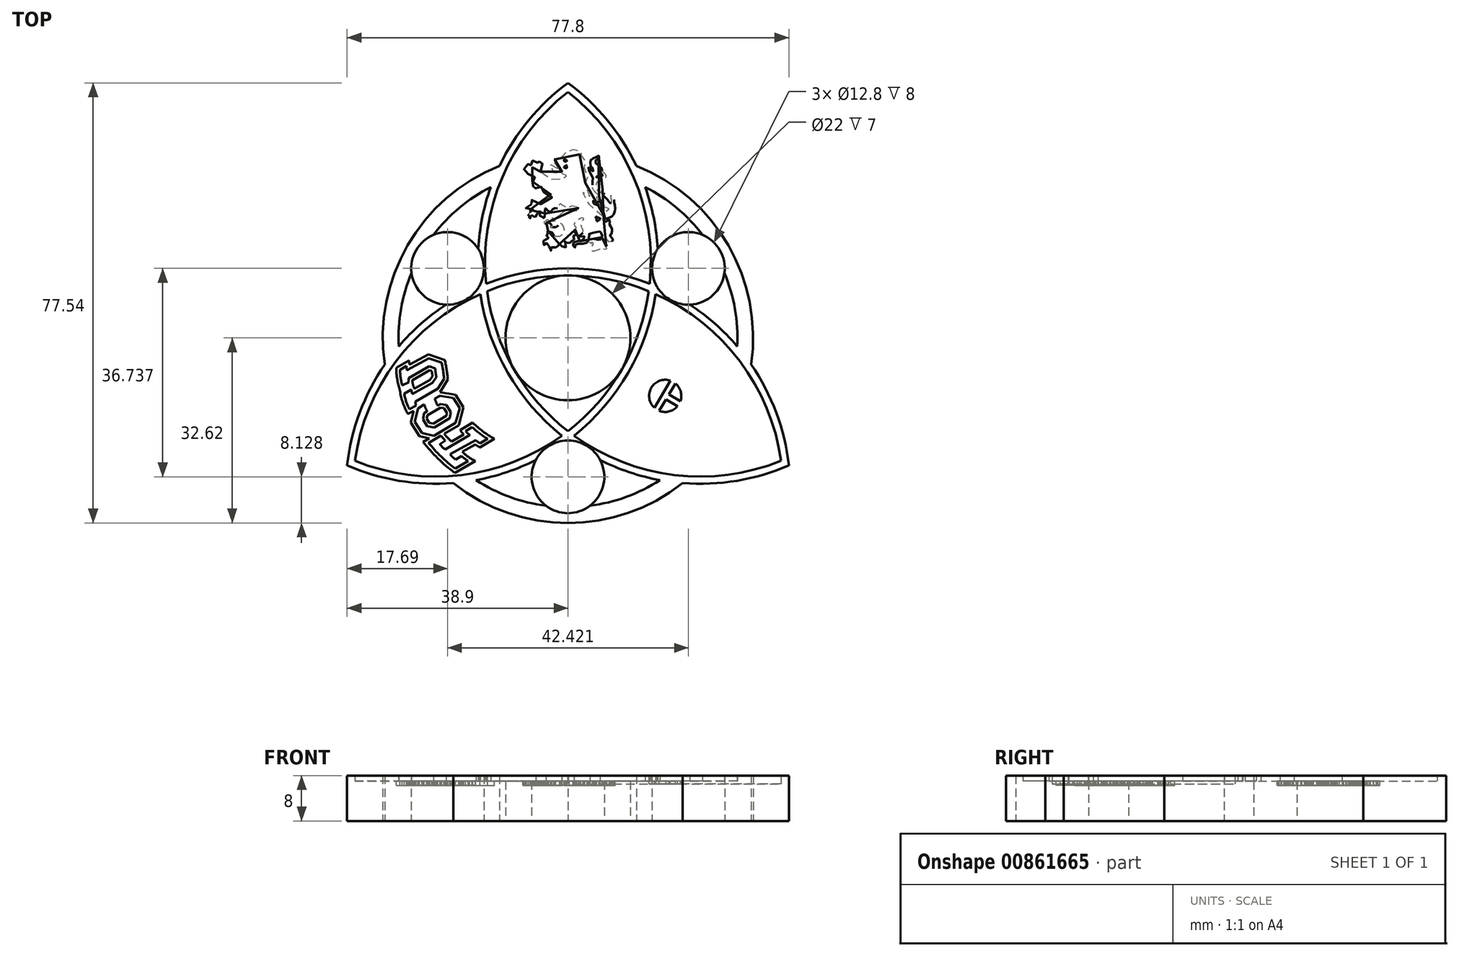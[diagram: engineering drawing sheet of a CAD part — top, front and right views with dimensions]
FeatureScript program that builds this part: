
annotation { "Feature Type Name" : "Feature", "Feature Type Description" : "" }
export const myFeature = defineFeature(function(context is Context, id is Id, definition is map)
    precondition{}
    {
        {
            var Q0;
            Q0=qCreatedBy(makeId("Top.planeOp"),FACE);
            var sketch = newSketch(context, id + "F0", { "sketchPlane" : qUnion([Q0])});
            skCircle(sketch, "E0", {"center": v(0, 0) * mm, "radius": 11 * mm});
            skArc(sketch, "E1", {"start": v(-13, 28.27) * mm, "mid": v(-26.95, 15.56) * mm, "end": v(-30.98, -2.89) * mm});
            skArc(sketch, "E2", {"start": v(0, 44.4) * mm, "mid": v(-7.94, 37.5) * mm, "end": v(-13, 28.27) * mm});
            skArc(sketch, "E3.MirrorCS", {"start": v(0, 44.4) * mm, "mid": v(7.94, 37.5) * mm, "end": v(13, 28.27) * mm});
            skArc(sketch, "E4.1.0", {"start": v(-38.45, -22.2) * mm, "mid": v(-28.5, -25.62) * mm, "end": v(-17.99, -25.39) * mm});
            skArc(sketch, "E4.1.1", {"start": v(-38.45, -22.2) * mm, "mid": v(-36.44, -11.88) * mm, "end": v(-30.98, -2.89) * mm});
            skArc(sketch, "E4.2.0", {"start": v(38.45, -22.2) * mm, "mid": v(36.44, -11.88) * mm, "end": v(30.98, -2.89) * mm});
            skArc(sketch, "E4.2.1", {"start": v(38.45, -22.2) * mm, "mid": v(28.5, -25.62) * mm, "end": v(17.99, -25.39) * mm});
            skArc(sketch, "E5.trimOffspring", {"start": v(-17.99, -25.39) * mm, "mid": v(0, -31.12) * mm, "end": v(17.99, -25.39) * mm});
            skArc(sketch, "E6.trimOffspring", {"start": v(30.98, -2.89) * mm, "mid": v(26.95, 15.56) * mm, "end": v(13, 28.27) * mm});
            skSolve(sketch);
        }
        {
            var Q0;
            Q0=qSketchRegion(id+"F0",true);
            extrude(context, id + "F1", {"entities" : qUnion([Q0]), "depth" : 7 * mm, "offsetDistance" : 25.4 * mm});
        }
        {
            var Q0;
            Q0=makeQuery(id+"F1.opExtrude","CAP_FACE",FACE,{"disambiguationData":[OSD([sQuery(id+"F0.wireOp",EDGE,"E0"),sQuery(id+"F0.wireOp",EDGE,"E1"),sQuery(id+"F0.wireOp",EDGE,"E2"),sQuery(id+"F0.wireOp",EDGE,"E3.MirrorCS"),sQuery(id+"F0.wireOp",EDGE,"E4.1.0"),sQuery(id+"F0.wireOp",EDGE,"E4.1.1"),sQuery(id+"F0.wireOp",EDGE,"E4.2.0"),sQuery(id+"F0.wireOp",EDGE,"E4.2.1"),sQuery(id+"F0.wireOp",EDGE,"E5.trimOffspring"),sQuery(id+"F0.wireOp",EDGE,"E6.trimOffspring")])],"isStart":false});
            var sketch = newSketch(context, id + "F2", { "sketchPlane" : qUnion([Q0])});
            skArc(sketch, "E7.0.1", {"start": v(-18.03, -25.36) * mm, "mid": v(0, -31.12) * mm, "end": v(18.03, -25.36) * mm});
            skArc(sketch, "E7.0.4", {"start": v(30.98, -2.94) * mm, "mid": v(26.95, 15.56) * mm, "end": v(12.95, 28.3) * mm});
            skArc(sketch, "E7.0.7", {"start": v(-12.95, 28.3) * mm, "mid": v(-26.95, 15.56) * mm, "end": v(-30.98, -2.94) * mm});
            skArc(sketch, "E8.2", {"start": v(-13.6, 26.56) * mm, "mid": v(-25.85, 14.92) * mm, "end": v(-29.8, -1.5) * mm});
            skArc(sketch, "E8.3", {"start": v(29.8, -1.5) * mm, "mid": v(25.85, 14.92) * mm, "end": v(13.6, 26.56) * mm});
            skArc(sketch, "E8.7", {"start": v(-16.2, -25.07) * mm, "mid": v(0, -29.85) * mm, "end": v(16.2, -25.07) * mm});
            skArc(sketch, "E9", {"start": v(0, 43.33) * mm, "mid": v(-11.57, 28.3) * mm, "end": v(-14.4, 9.53) * mm});
            skArc(sketch, "E10", {"start": v(-37.52, -21.66) * mm, "mid": v(-18.71, -24.17) * mm, "end": v(-1.05, -17.23) * mm});
            skArc(sketch, "E11", {"start": v(37.52, -21.66) * mm, "mid": v(30.29, -4.12) * mm, "end": v(15.45, 7.7) * mm});
            skArc(sketch, "E12.0", {"start": v(0, 44.92) * mm, "mid": v(-7.61, 37.5) * mm, "end": v(-12.95, 28.3) * mm});
            skArc(sketch, "E13.0", {"start": v(-38.9, -22.46) * mm, "mid": v(-28.67, -25.34) * mm, "end": v(-18.03, -25.36) * mm});
            skArc(sketch, "E14.0", {"start": v(38.9, -22.46) * mm, "mid": v(36.28, -12.16) * mm, "end": v(30.98, -2.94) * mm});
            skPoint(sketch, "E15.orphan", {"position": v(-13, 28.27) * mm});
            skPoint(sketch, "E16.orphan", {"position": v(13, 28.27) * mm});
            skArc(sketch, "E17.trimOffspring", {"start": v(-13.6, 26.56) * mm, "mid": v(-15.62, 17.9) * mm, "end": v(-15.62, 9.02) * mm});
            skArc(sketch, "E18.trimOffspring", {"start": v(12.95, 28.3) * mm, "mid": v(7.61, 37.5) * mm, "end": v(0, 44.92) * mm});
            skArc(sketch, "E19.trimOffspring", {"start": v(-15.62, 9.02) * mm, "mid": v(-23.32, 4.57) * mm, "end": v(-29.8, -1.5) * mm});
            skArc(sketch, "E20.trimOffspring", {"start": v(-15.45, 7.7) * mm, "mid": v(-30.29, -4.12) * mm, "end": v(-37.52, -21.66) * mm});
            skArc(sketch, "E21.trimOffspring", {"start": v(-15.45, 7.7) * mm, "mid": v(-10.63, -6.14) * mm, "end": v(-1.05, -17.23) * mm});
            skArc(sketch, "E22.trimOffspring", {"start": v(-14.24, 8.22) * mm, "mid": v(-9.53, -5.5) * mm, "end": v(0, -16.44) * mm});
            skArc(sketch, "E23.trimOffspring", {"start": v(14.4, 9.53) * mm, "mid": v(11.57, 28.3) * mm, "end": v(0, 43.33) * mm});
            skArc(sketch, "E24.trimOffspring", {"start": v(14.4, 9.53) * mm, "mid": v(0, 12.27) * mm, "end": v(-14.4, 9.53) * mm});
            skArc(sketch, "E25.trimOffspring", {"start": v(14.24, 8.22) * mm, "mid": v(0, 11) * mm, "end": v(-14.24, 8.22) * mm});
            skArc(sketch, "E26.trimOffspring", {"start": v(15.62, 9.02) * mm, "mid": v(15.62, 17.9) * mm, "end": v(13.6, 26.56) * mm});
            skArc(sketch, "E27.trimOffspring", {"start": v(0, -18.04) * mm, "mid": v(7.7, -22.48) * mm, "end": v(16.2, -25.07) * mm});
            skArc(sketch, "E28.trimOffspring", {"start": v(0, -16.44) * mm, "mid": v(9.53, -5.5) * mm, "end": v(14.24, 8.22) * mm});
            skArc(sketch, "E29.trimOffspring", {"start": v(1.05, -17.23) * mm, "mid": v(18.71, -24.17) * mm, "end": v(37.52, -21.66) * mm});
            skArc(sketch, "E30.trimOffspring", {"start": v(1.05, -17.23) * mm, "mid": v(10.63, -6.14) * mm, "end": v(15.45, 7.7) * mm});
            skPoint(sketch, "E31.orphan", {"position": v(-30.98, -2.89) * mm});
            skPoint(sketch, "E32.orphan", {"position": v(-17.99, -25.39) * mm});
            skArc(sketch, "E33.trimOffspring", {"start": v(-30.98, -2.94) * mm, "mid": v(-36.28, -12.16) * mm, "end": v(-38.9, -22.46) * mm});
            skArc(sketch, "E34.trimOffspring", {"start": v(-16.2, -25.07) * mm, "mid": v(-7.7, -22.48) * mm, "end": v(0, -18.04) * mm});
            skPoint(sketch, "E35.orphan", {"position": v(30.98, -2.89) * mm});
            skPoint(sketch, "E36.orphan", {"position": v(17.99, -25.39) * mm});
            skArc(sketch, "E37.trimOffspring", {"start": v(18.03, -25.36) * mm, "mid": v(28.67, -25.34) * mm, "end": v(38.9, -22.46) * mm});
            skArc(sketch, "E38.trimOffspring", {"start": v(29.8, -1.5) * mm, "mid": v(23.32, 4.57) * mm, "end": v(15.62, 9.02) * mm});
            skSolve(sketch);
        }
        {
            var Q0;
            Q0=qSketchRegion(id+"F2",true);
            extrude(context, id + "F3", {"entities" : qUnion([Q0]), "operationType" : NewBodyOperationType.ADD, "depth" : 1 * mm, "offsetDistance" : 25.4 * mm});
        }
        {
            var Q0;
            Q0=makeQuery(id+"F3.boolean.opBoolean","SPLIT",FACE,{"disambiguationData":[TD([makeQuery(id+"F3.opExtrude","SWEPT_FACE",FACE,{"disambiguationData":[OSD([sQuery(id+"F2.wireOp",EDGE,"E10")])]}),makeQuery(id+"F3.opExtrude","SWEPT_FACE",FACE,{"disambiguationData":[OSD([sQuery(id+"F2.wireOp",EDGE,"E20.trimOffspring")])]}),makeQuery(id+"F3.opExtrude","SWEPT_FACE",FACE,{"disambiguationData":[OSD([sQuery(id+"F2.wireOp",EDGE,"E21.trimOffspring")])]})])],"derivedFrom":makeQuery(id+"F1.opExtrude","CAP_FACE",FACE,{"disambiguationData":[OSD([sQuery(id+"F0.wireOp",EDGE,"E0"),sQuery(id+"F0.wireOp",EDGE,"E1"),sQuery(id+"F0.wireOp",EDGE,"E2"),sQuery(id+"F0.wireOp",EDGE,"E3.MirrorCS"),sQuery(id+"F0.wireOp",EDGE,"E4.1.0"),sQuery(id+"F0.wireOp",EDGE,"E4.1.1"),sQuery(id+"F0.wireOp",EDGE,"E4.2.0"),sQuery(id+"F0.wireOp",EDGE,"E4.2.1"),sQuery(id+"F0.wireOp",EDGE,"E5.trimOffspring"),sQuery(id+"F0.wireOp",EDGE,"E6.trimOffspring")])],"isStart":false})});
            var sketch = newSketch(context, id + "F4", { "sketchPlane" : qUnion([Q0])});
            skArc(sketch, "E39.0.0", {"start": v(-37.99, -17.38) * mm, "mid": v(-35.23, -9.8) * mm, "end": v(-30.98, -2.94) * mm});
            skArc(sketch, "E39.0.1", {"start": v(-30.98, -2.94) * mm, "mid": v(-30.98, -2.91) * mm, "end": v(-30.98, -2.89) * mm});
            skArc(sketch, "E39.0.2", {"start": v(-30.98, -2.89) * mm, "mid": v(-35.48, -9.65) * mm, "end": v(-37.99, -17.38) * mm});
            skArc(sketch, "E40.0.0", {"start": v(-17.99, -25.39) * mm, "mid": v(-18.01, -25.37) * mm, "end": v(-18.03, -25.36) * mm});
            skArc(sketch, "E40.0.1", {"start": v(-18.03, -25.36) * mm, "mid": v(-26.1, -25.61) * mm, "end": v(-34.05, -24.2) * mm});
            skArc(sketch, "E40.0.2", {"start": v(-34.05, -24.2) * mm, "mid": v(-26.1, -25.9) * mm, "end": v(-17.99, -25.39) * mm});
            skArc(sketch, "E41.0.0", {"start": v(34.05, -24.2) * mm, "mid": v(26.1, -25.61) * mm, "end": v(18.03, -25.36) * mm});
            skArc(sketch, "E41.0.1", {"start": v(18.03, -25.36) * mm, "mid": v(18.01, -25.37) * mm, "end": v(17.99, -25.39) * mm});
            skArc(sketch, "E41.0.2", {"start": v(17.99, -25.39) * mm, "mid": v(26.1, -25.9) * mm, "end": v(34.05, -24.2) * mm});
            skArc(sketch, "E42.0.0", {"start": v(30.98, -2.89) * mm, "mid": v(30.98, -2.91) * mm, "end": v(30.98, -2.94) * mm});
            skArc(sketch, "E42.0.1", {"start": v(30.98, -2.94) * mm, "mid": v(35.23, -9.8) * mm, "end": v(37.99, -17.38) * mm});
            skArc(sketch, "E42.0.2", {"start": v(37.99, -17.38) * mm, "mid": v(35.48, -9.65) * mm, "end": v(30.98, -2.89) * mm});
            skArc(sketch, "E43.0.0", {"start": v(12.95, 28.3) * mm, "mid": v(12.97, 28.28) * mm, "end": v(13, 28.27) * mm});
            skArc(sketch, "E43.0.1", {"start": v(13, 28.27) * mm, "mid": v(9.38, 35.55) * mm, "end": v(3.94, 41.59) * mm});
            skArc(sketch, "E43.0.2", {"start": v(3.94, 41.59) * mm, "mid": v(9.13, 35.4) * mm, "end": v(12.95, 28.3) * mm});
            skArc(sketch, "E44.0.0", {"start": v(-13, 28.27) * mm, "mid": v(-12.97, 28.28) * mm, "end": v(-12.95, 28.3) * mm});
            skArc(sketch, "E44.0.1", {"start": v(-12.95, 28.3) * mm, "mid": v(-9.13, 35.4) * mm, "end": v(-3.94, 41.59) * mm});
            skArc(sketch, "E44.0.2", {"start": v(-3.94, 41.59) * mm, "mid": v(-9.38, 35.55) * mm, "end": v(-13, 28.27) * mm});
            skSolve(sketch);
        }
        {
            var Q0;
            Q0=qSketchRegion(id+"F4",true);
            extrude(context, id + "F5", {"entities" : qUnion([Q0]), "operationType" : NewBodyOperationType.REMOVE, "oppositeDirection" : true, "depth" : 25.4 * mm, "offsetDistance" : 25.4 * mm});
        }
        {
            var Q0;
            {var subQ0=sQuery(id+"F2.wireOp",EDGE,"E13.0");var subQ2=sQuery(id+"F0.wireOp",EDGE,"E4.1.0");var subQ3=sQuery(id+"F2.wireOp",EDGE,"E33.trimOffspring");Q0=makeQuery(id+"F3.boolean.opBoolean","SPLIT",FACE,{"disambiguationData":[TD([makeQuery(id+"F1.opExtrude","SWEPT_FACE",FACE,{"disambiguationData":[OSD([subQ2])]})])],"derivedFrom":makeQuery(id+"F3.opExtrude","CAP_FACE",FACE,{"disambiguationData":[OSD([sQuery(id+"F2.wireOp",EDGE,"E7.0.1"),sQuery(id+"F2.wireOp",EDGE,"E7.0.4"),sQuery(id+"F2.wireOp",EDGE,"E7.0.7"),sQuery(id+"F2.wireOp",EDGE,"E8.2"),sQuery(id+"F2.wireOp",EDGE,"E8.3"),sQuery(id+"F2.wireOp",EDGE,"E8.7"),sQuery(id+"F2.wireOp",EDGE,"E9"),sQuery(id+"F2.wireOp",EDGE,"E10"),sQuery(id+"F2.wireOp",EDGE,"E11"),sQuery(id+"F2.wireOp",EDGE,"E12.0"),subQ0,sQuery(id+"F2.wireOp",EDGE,"E14.0"),sQuery(id+"F2.wireOp",EDGE,"E17.trimOffspring"),sQuery(id+"F2.wireOp",EDGE,"E18.trimOffspring"),sQuery(id+"F2.wireOp",EDGE,"E19.trimOffspring"),sQuery(id+"F2.wireOp",EDGE,"E20.trimOffspring"),sQuery(id+"F2.wireOp",EDGE,"E21.trimOffspring"),sQuery(id+"F2.wireOp",EDGE,"E22.trimOffspring"),sQuery(id+"F2.wireOp",EDGE,"E23.trimOffspring"),sQuery(id+"F2.wireOp",EDGE,"E24.trimOffspring"),sQuery(id+"F2.wireOp",EDGE,"E25.trimOffspring"),sQuery(id+"F2.wireOp",EDGE,"E26.trimOffspring"),sQuery(id+"F2.wireOp",EDGE,"E27.trimOffspring"),sQuery(id+"F2.wireOp",EDGE,"E28.trimOffspring"),sQuery(id+"F2.wireOp",EDGE,"E29.trimOffspring"),sQuery(id+"F2.wireOp",EDGE,"E30.trimOffspring"),subQ3,sQuery(id+"F2.wireOp",EDGE,"E34.trimOffspring"),sQuery(id+"F2.wireOp",EDGE,"E37.trimOffspring"),sQuery(id+"F2.wireOp",EDGE,"E38.trimOffspring")])],"isStart":true})});}
            var sketch = newSketch(context, id + "F6", { "sketchPlane" : qUnion([Q0])});
            skArc(sketch, "E45.0.0", {"start": v(-37.99, 17.38) * mm, "mid": v(-38.32, 19.78) * mm, "end": v(-38.45, 22.2) * mm});
            skArc(sketch, "E45.0.1", {"start": v(-38.45, 22.2) * mm, "mid": v(-36.3, 23.3) * mm, "end": v(-34.05, 24.2) * mm});
            skArc(sketch, "E45.0.2", {"start": v(-34.05, 24.2) * mm, "mid": v(-36.5, 23.41) * mm, "end": v(-38.9, 22.46) * mm});
            skArc(sketch, "E45.0.3", {"start": v(-38.9, 22.46) * mm, "mid": v(-38.53, 19.9) * mm, "end": v(-37.99, 17.38) * mm});
            skArc(sketch, "E46.0.0", {"start": v(34.05, 24.2) * mm, "mid": v(36.3, 23.3) * mm, "end": v(38.45, 22.2) * mm});
            skArc(sketch, "E46.0.1", {"start": v(38.45, 22.2) * mm, "mid": v(38.32, 19.78) * mm, "end": v(37.99, 17.38) * mm});
            skArc(sketch, "E46.0.2", {"start": v(37.99, 17.38) * mm, "mid": v(38.53, 19.9) * mm, "end": v(38.9, 22.46) * mm});
            skArc(sketch, "E46.0.3", {"start": v(38.9, 22.46) * mm, "mid": v(36.5, 23.41) * mm, "end": v(34.05, 24.2) * mm});
            skArc(sketch, "E47.0.0", {"start": v(3.94, -41.59) * mm, "mid": v(2.03, -43.07) * mm, "end": v(0, -44.4) * mm});
            skArc(sketch, "E47.0.1", {"start": v(0, -44.4) * mm, "mid": v(-2.03, -43.07) * mm, "end": v(-3.94, -41.59) * mm});
            skArc(sketch, "E47.0.2", {"start": v(-3.94, -41.59) * mm, "mid": v(-2.02, -43.32) * mm, "end": v(0, -44.92) * mm});
            skArc(sketch, "E47.0.3", {"start": v(0, -44.92) * mm, "mid": v(2.02, -43.32) * mm, "end": v(3.94, -41.59) * mm});
            skSolve(sketch);
        }
        {
            var Q0;
            Q0=qSketchRegion(id+"F6",true);
            extrude(context, id + "F7", {"entities" : qUnion([Q0]), "operationType" : NewBodyOperationType.ADD, "depth" : 7 * mm, "offsetDistance" : 25.4 * mm});
        }
        {
            var Q0;
            Q0=makeQuery(id+"F3.boolean.opBoolean","SPLIT",FACE,{"disambiguationData":[TD([makeQuery(id+"F3.opExtrude","SWEPT_FACE",FACE,{"disambiguationData":[OSD([sQuery(id+"F2.wireOp",EDGE,"E8.2")])]}),makeQuery(id+"F3.opExtrude","SWEPT_FACE",FACE,{"disambiguationData":[OSD([sQuery(id+"F2.wireOp",EDGE,"E17.trimOffspring")])]}),makeQuery(id+"F3.opExtrude","SWEPT_FACE",FACE,{"disambiguationData":[OSD([sQuery(id+"F2.wireOp",EDGE,"E19.trimOffspring")])]})])],"derivedFrom":makeQuery(id+"F1.opExtrude","CAP_FACE",FACE,{"disambiguationData":[OSD([sQuery(id+"F0.wireOp",EDGE,"E0"),sQuery(id+"F0.wireOp",EDGE,"E1"),sQuery(id+"F0.wireOp",EDGE,"E2"),sQuery(id+"F0.wireOp",EDGE,"E3.MirrorCS"),sQuery(id+"F0.wireOp",EDGE,"E4.1.0"),sQuery(id+"F0.wireOp",EDGE,"E4.1.1"),sQuery(id+"F0.wireOp",EDGE,"E4.2.0"),sQuery(id+"F0.wireOp",EDGE,"E4.2.1"),sQuery(id+"F0.wireOp",EDGE,"E5.trimOffspring"),sQuery(id+"F0.wireOp",EDGE,"E6.trimOffspring")])],"isStart":false})});
            var sketch = newSketch(context, id + "F8", { "sketchPlane" : qUnion([Q0])});
            skPoint(sketch, "E48.first.point", {"position": v(-25.85, 14.92) * mm});
            skPoint(sketch, "E48.second.point", {"position": v(-15.86, 12.39) * mm});
            skPoint(sketch, "E48.third.point", {"position": v(-18.66, 7.54) * mm});
            skPoint(sketch, "E49.center", {"position": v(0, 0) * mm});
            skCircle(sketch, "E50", {"center": v(-21.21, 12.25) * mm, "radius": 6.25 * mm});
            skCircle(sketch, "E51.1.0", {"center": v(0, -24.5) * mm, "radius": 6.25 * mm});
            skCircle(sketch, "E51.2.0", {"center": v(21.21, 12.25) * mm, "radius": 6.25 * mm});
            skSolve(sketch);
        }
        {
            var Q0;
            Q0=qSketchRegion(id+"F8",true);
            extrude(context, id + "F9", {"entities" : qUnion([Q0]), "operationType" : NewBodyOperationType.REMOVE, "oppositeDirection" : true, "depth" : 25.4 * mm, "offsetDistance" : 25.4 * mm, "hasSecondDirection" : true, "secondDirectionOppositeDirection" : false, "secondDirectionDepth" : 25.4 * mm});
        }
        {
            var Q0;
            Q0=makeQuery(id+"F3.boolean.opBoolean","SPLIT",FACE,{"disambiguationData":[TD([makeQuery(id+"F3.opExtrude","SWEPT_FACE",FACE,{"disambiguationData":[OSD([sQuery(id+"F2.wireOp",EDGE,"E10")])]}),makeQuery(id+"F3.opExtrude","SWEPT_FACE",FACE,{"disambiguationData":[OSD([sQuery(id+"F2.wireOp",EDGE,"E20.trimOffspring")])]}),makeQuery(id+"F3.opExtrude","SWEPT_FACE",FACE,{"disambiguationData":[OSD([sQuery(id+"F2.wireOp",EDGE,"E21.trimOffspring")])]})])],"derivedFrom":makeQuery(id+"F1.opExtrude","CAP_FACE",FACE,{"disambiguationData":[OSD([sQuery(id+"F0.wireOp",EDGE,"E0"),sQuery(id+"F0.wireOp",EDGE,"E1"),sQuery(id+"F0.wireOp",EDGE,"E2"),sQuery(id+"F0.wireOp",EDGE,"E3.MirrorCS"),sQuery(id+"F0.wireOp",EDGE,"E4.1.0"),sQuery(id+"F0.wireOp",EDGE,"E4.1.1"),sQuery(id+"F0.wireOp",EDGE,"E4.2.0"),sQuery(id+"F0.wireOp",EDGE,"E4.2.1"),sQuery(id+"F0.wireOp",EDGE,"E5.trimOffspring"),sQuery(id+"F0.wireOp",EDGE,"E6.trimOffspring")])],"isStart":false})});
            var sketch = newSketch(context, id + "F10", { "sketchPlane" : qUnion([Q0])});
            skLineSegment(sketch, "E52", {"start": v(-17.6, -21.7) * mm, "end": v(-19.9, -23.04) * mm});
            skLineSegment(sketch, "E53", {"start": v(-24.55, -18.5) * mm, "end": v(-22.36, -17.22) * mm});
            skLineSegment(sketch, "E54", {"start": v(-21.59, -18.12) * mm, "end": v(-22.57, -18.74) * mm});
            skLineSegment(sketch, "E55", {"start": v(-21.67, -19.67) * mm, "end": v(-17.32, -17.12) * mm});
            skLineSegment(sketch, "E56", {"start": v(-18.04, -16.44) * mm, "end": v(-16.86, -15.73) * mm});
            skLineSegment(sketch, "E57", {"start": v(-18.74, -20.8) * mm, "end": v(-19.82, -21.45) * mm});
            skLineSegment(sketch, "E58", {"start": v(-20.77, -20.53) * mm, "end": v(-16.28, -18) * mm});
            skLineSegment(sketch, "E59", {"start": v(-15.49, -18.58) * mm, "end": v(-14.18, -17.8) * mm});
            skArc(sketch, "E60", {"start": v(-24.55, -18.5) * mm, "mid": v(-22.35, -20.9) * mm, "end": v(-19.9, -23.04) * mm});
            skArc(sketch, "E61", {"start": v(-20.77, -20.53) * mm, "mid": v(-20.31, -21) * mm, "end": v(-19.82, -21.45) * mm});
            skArc(sketch, "E62", {"start": v(-22.57, -18.74) * mm, "mid": v(-22.14, -19.23) * mm, "end": v(-21.67, -19.67) * mm});
            skArc(sketch, "E63", {"start": v(-22.36, -17.22) * mm, "mid": v(-21.99, -17.68) * mm, "end": v(-21.59, -18.12) * mm});
            skArc(sketch, "E64", {"start": v(-18.74, -20.8) * mm, "mid": v(-18.2, -21.28) * mm, "end": v(-17.6, -21.7) * mm});
            skArc(sketch, "E65", {"start": v(-16.86, -15.73) * mm, "mid": v(-15.57, -16.83) * mm, "end": v(-14.18, -17.8) * mm});
            skArc(sketch, "E66", {"start": v(-18.04, -16.44) * mm, "mid": v(-17.7, -16.8) * mm, "end": v(-17.32, -17.12) * mm});
            skArc(sketch, "E67", {"start": v(-16.28, -18) * mm, "mid": v(-15.9, -18.31) * mm, "end": v(-15.49, -18.58) * mm});
            skLineSegment(sketch, "E68", {"start": v(-23.65, -17.24) * mm, "end": v(-25.73, -16.75) * mm});
            skLineSegment(sketch, "E69", {"start": v(-25.73, -16.75) * mm, "end": v(-27.01, -14.79) * mm});
            skLineSegment(sketch, "E70", {"start": v(-27.01, -14.79) * mm, "end": v(-26.44, -12.43) * mm});
            skLineSegment(sketch, "E71", {"start": v(-26.44, -12.43) * mm, "end": v(-25.31, -11.75) * mm});
            skLineSegment(sketch, "E72", {"start": v(-23.65, -17.24) * mm, "end": v(-19.8, -15) * mm});
            skLineSegment(sketch, "E73", {"start": v(-23.47, -10.71) * mm, "end": v(-22.56, -10.2) * mm});
            skLineSegment(sketch, "E74", {"start": v(-22.56, -10.2) * mm, "end": v(-20.2, -10.62) * mm});
            skLineSegment(sketch, "E75", {"start": v(-19.8, -15) * mm, "end": v(-19.07, -12.37) * mm});
            skLineSegment(sketch, "E76", {"start": v(-22.93, -11.93) * mm, "end": v(-22.47, -11.67) * mm});
            skLineSegment(sketch, "E77", {"start": v(-22.47, -11.67) * mm, "end": v(-21.46, -11.8) * mm});
            skLineSegment(sketch, "E78", {"start": v(-20.85, -14.13) * mm, "end": v(-23.58, -15.8) * mm});
            skLineSegment(sketch, "E79", {"start": v(-23.58, -15.8) * mm, "end": v(-24.84, -15.55) * mm});
            skLineSegment(sketch, "E80", {"start": v(-24.84, -15.55) * mm, "end": v(-25.54, -14.34) * mm});
            skLineSegment(sketch, "E81", {"start": v(-25.54, -14.34) * mm, "end": v(-25.31, -13.24) * mm});
            skLineSegment(sketch, "E82", {"start": v(-25.31, -13.24) * mm, "end": v(-24.8, -12.94) * mm});
            skArc(sketch, "E83", {"start": v(-23.47, -10.71) * mm, "mid": v(-23.23, -11.34) * mm, "end": v(-22.93, -11.93) * mm});
            skArc(sketch, "E84", {"start": v(-25.31, -11.75) * mm, "mid": v(-25.09, -12.36) * mm, "end": v(-24.8, -12.94) * mm});
            skLineSegment(sketch, "E85", {"start": v(-20.85, -14.13) * mm, "end": v(-20.66, -13.06) * mm});
            skLineSegment(sketch, "E86", {"start": v(-20.66, -13.06) * mm, "end": v(-21.46, -11.8) * mm});
            skLineSegment(sketch, "E87", {"start": v(-19.07, -12.37) * mm, "end": v(-20.2, -10.62) * mm});
            skLineSegment(sketch, "E88", {"start": v(-28.86, -9.85) * mm, "end": v(-27.6, -9.12) * mm});
            skLineSegment(sketch, "E89", {"start": v(-29.2, -8.4) * mm, "end": v(-28.03, -7.78) * mm});
            skLineSegment(sketch, "E90", {"start": v(-27.93, -12.55) * mm, "end": v(-26.75, -11.9) * mm});
            skLineSegment(sketch, "E91", {"start": v(-29.6, -5.64) * mm, "end": v(-28.44, -4.95) * mm});
            skLineSegment(sketch, "E92", {"start": v(-26.86, -11.2) * mm, "end": v(-22.92, -8.95) * mm});
            skLineSegment(sketch, "E93", {"start": v(-22.92, -8.95) * mm, "end": v(-21.8, -7.14) * mm});
            skLineSegment(sketch, "E94", {"start": v(-22.23, -4.4) * mm, "end": v(-24.51, -3.58) * mm});
            skLineSegment(sketch, "E95", {"start": v(-24.51, -3.58) * mm, "end": v(-28.36, -5.68) * mm});
            skLineSegment(sketch, "E96", {"start": v(-27.43, -9.87) * mm, "end": v(-23.85, -7.9) * mm});
            skLineSegment(sketch, "E97", {"start": v(-23.85, -7.9) * mm, "end": v(-23.18, -6.92) * mm});
            skLineSegment(sketch, "E98", {"start": v(-23.4, -5.4) * mm, "end": v(-24.42, -4.99) * mm});
            skLineSegment(sketch, "E99", {"start": v(-24.42, -4.99) * mm, "end": v(-28.05, -7.1) * mm});
            skArc(sketch, "E100", {"start": v(-28.86, -9.85) * mm, "mid": v(-28.48, -11.23) * mm, "end": v(-27.93, -12.55) * mm});
            skArc(sketch, "E101", {"start": v(-29.6, -5.64) * mm, "mid": v(-29.47, -7.03) * mm, "end": v(-29.2, -8.4) * mm});
            skArc(sketch, "E102", {"start": v(-28.05, -7.1) * mm, "mid": v(-28.06, -7.44) * mm, "end": v(-28.03, -7.78) * mm});
            skArc(sketch, "E103", {"start": v(-28.44, -4.95) * mm, "mid": v(-28.43, -5.32) * mm, "end": v(-28.36, -5.68) * mm});
            skArc(sketch, "E104", {"start": v(-26.86, -11.2) * mm, "mid": v(-26.84, -11.55) * mm, "end": v(-26.75, -11.9) * mm});
            skArc(sketch, "E105", {"start": v(-27.6, -9.12) * mm, "mid": v(-27.53, -9.5) * mm, "end": v(-27.43, -9.87) * mm});
            skArc(sketch, "E106", {"start": v(-23.4, -5.4) * mm, "mid": v(-23.3, -6.16) * mm, "end": v(-23.18, -6.92) * mm});
            skArc(sketch, "E107", {"start": v(-21.8, -7.14) * mm, "mid": v(-22, -5.77) * mm, "end": v(-22.23, -4.4) * mm});
            skArc(sketch, "E108.0", {"start": v(-21.8, -16.9) * mm, "mid": v(-21.2, -17.61) * mm, "end": v(-20.52, -18.26) * mm});
            skArc(sketch, "E109.0", {"start": v(-18.97, -16.26) * mm, "mid": v(-18.69, -16.65) * mm, "end": v(-18.38, -17) * mm});
            skLineSegment(sketch, "E110.0", {"start": v(-18.97, -16.26) * mm, "end": v(-16.77, -14.93) * mm});
            skArc(sketch, "E111.0", {"start": v(-16.77, -14.93) * mm, "mid": v(-14.96, -16.5) * mm, "end": v(-12.94, -17.78) * mm});
            skLineSegment(sketch, "E112.0", {"start": v(-15.47, -19.3) * mm, "end": v(-12.94, -17.78) * mm});
            skArc(sketch, "E113.0", {"start": v(-16.34, -18.77) * mm, "mid": v(-15.92, -19.06) * mm, "end": v(-15.47, -19.3) * mm});
            skLineSegment(sketch, "E114.0", {"start": v(-18.6, -20.04) * mm, "end": v(-16.34, -18.77) * mm});
            skArc(sketch, "E115.0", {"start": v(-18.6, -20.04) * mm, "mid": v(-17.54, -20.98) * mm, "end": v(-16.32, -21.69) * mm});
            skLineSegment(sketch, "E116.0", {"start": v(-16.32, -21.69) * mm, "end": v(-19.95, -23.8) * mm});
            skArc(sketch, "E117.0", {"start": v(-25.5, -18.33) * mm, "mid": v(-22.9, -21.25) * mm, "end": v(-19.95, -23.8) * mm});
            skLineSegment(sketch, "E118.0", {"start": v(-25.5, -18.33) * mm, "end": v(-24.44, -17.7) * mm});
            skLineSegment(sketch, "E119.0", {"start": v(-24.44, -17.7) * mm, "end": v(-26.13, -17.31) * mm});
            skLineSegment(sketch, "E120.trimOffspring", {"start": v(-20.52, -18.26) * mm, "end": v(-18.38, -17) * mm});
            skLineSegment(sketch, "E121.0", {"start": v(-21.8, -16.9) * mm, "end": v(-19.25, -15.42) * mm});
            skLineSegment(sketch, "E122.0", {"start": v(-26.13, -17.31) * mm, "end": v(-27.7, -14.9) * mm});
            skLineSegment(sketch, "E123.0", {"start": v(-27.7, -14.9) * mm, "end": v(-27.2, -12.87) * mm});
            skLineSegment(sketch, "E124.0", {"start": v(-28.18, -13.41) * mm, "end": v(-27.2, -12.87) * mm});
            skArc(sketch, "E125.0", {"start": v(-29.59, -9.34) * mm, "mid": v(-29.08, -11.44) * mm, "end": v(-28.18, -13.41) * mm});
            skLineSegment(sketch, "E126.0", {"start": v(-27.06, -8.94) * mm, "end": v(-24.3, -7.42) * mm});
            skLineSegment(sketch, "E127.0", {"start": v(-24.3, -7.42) * mm, "end": v(-23.85, -6.78) * mm});
            skArc(sketch, "E128.0", {"start": v(-23.98, -5.85) * mm, "mid": v(-23.92, -6.31) * mm, "end": v(-23.85, -6.78) * mm});
            skLineSegment(sketch, "E129.0", {"start": v(-23.98, -5.85) * mm, "end": v(-24.37, -5.7) * mm});
            skLineSegment(sketch, "E130.0", {"start": v(-24.37, -5.7) * mm, "end": v(-27.42, -7.47) * mm});
            skArc(sketch, "E131.0", {"start": v(-30.25, -5.29) * mm, "mid": v(-30.06, -7.34) * mm, "end": v(-29.59, -9.34) * mm});
            skLineSegment(sketch, "E132.0", {"start": v(-30.25, -5.29) * mm, "end": v(-28.02, -3.97) * mm});
            skLineSegment(sketch, "E133.0", {"start": v(-24.57, -2.89) * mm, "end": v(-27.88, -4.7) * mm});
            skLineSegment(sketch, "E134.0", {"start": v(-21.67, -3.92) * mm, "end": v(-24.57, -2.89) * mm});
            skArc(sketch, "E135.0", {"start": v(-21.15, -7.28) * mm, "mid": v(-21.38, -5.6) * mm, "end": v(-21.67, -3.92) * mm});
            skLineSegment(sketch, "E136.0", {"start": v(-22.55, -9.55) * mm, "end": v(-21.15, -7.28) * mm});
            skLineSegment(sketch, "E137.0", {"start": v(-22.55, -9.55) * mm, "end": v(-19.8, -10.05) * mm});
            skLineSegment(sketch, "E138.0", {"start": v(-18.38, -12.27) * mm, "end": v(-19.8, -10.05) * mm});
            skLineSegment(sketch, "E139.0", {"start": v(-19.25, -15.42) * mm, "end": v(-18.38, -12.27) * mm});
            skArc(sketch, "E140", {"start": v(-27.42, -7.47) * mm, "mid": v(-27.3, -8.22) * mm, "end": v(-27.06, -8.94) * mm});
            skArc(sketch, "E141", {"start": v(-28.02, -3.97) * mm, "mid": v(-27.98, -4.33) * mm, "end": v(-27.88, -4.7) * mm});
            skLineSegment(sketch, "E142.0", {"start": v(-24.75, -13.64) * mm, "end": v(-22.45, -12.31) * mm});
            skLineSegment(sketch, "E143.0", {"start": v(-24.87, -14.23) * mm, "end": v(-24.75, -13.64) * mm});
            skLineSegment(sketch, "E144.0", {"start": v(-24.44, -14.98) * mm, "end": v(-24.87, -14.23) * mm});
            skLineSegment(sketch, "E145.0", {"start": v(-23.7, -15.12) * mm, "end": v(-24.44, -14.98) * mm});
            skLineSegment(sketch, "E146.0", {"start": v(-21.42, -13.73) * mm, "end": v(-23.7, -15.12) * mm});
            skLineSegment(sketch, "E147.0", {"start": v(-21.42, -13.73) * mm, "end": v(-21.33, -13.19) * mm});
            skLineSegment(sketch, "E148.0", {"start": v(-21.33, -13.19) * mm, "end": v(-21.84, -12.39) * mm});
            skLineSegment(sketch, "E149.0", {"start": v(-22.45, -12.31) * mm, "end": v(-21.84, -12.39) * mm});
            skSolve(sketch);
        }
        {
            var Q0;
            Q0=qSketchRegion(id+"F10",true);
            extrude(context, id + "F11", {"entities" : qUnion([Q0]), "operationType" : NewBodyOperationType.REMOVE, "oppositeDirection" : true, "depth" : .75 * mm, "offsetDistance" : 25.4 * mm});
        }
        {
            var Q0;
            Q0=makeQuery(id+"F3.boolean.opBoolean","SPLIT",FACE,{"disambiguationData":[TD([makeQuery(id+"F3.opExtrude","SWEPT_FACE",FACE,{"disambiguationData":[OSD([sQuery(id+"F2.wireOp",EDGE,"E9")])]}),makeQuery(id+"F3.opExtrude","SWEPT_FACE",FACE,{"disambiguationData":[OSD([sQuery(id+"F2.wireOp",EDGE,"E23.trimOffspring")])]}),makeQuery(id+"F3.opExtrude","SWEPT_FACE",FACE,{"disambiguationData":[OSD([sQuery(id+"F2.wireOp",EDGE,"E24.trimOffspring")])]})])],"derivedFrom":makeQuery(id+"F1.opExtrude","CAP_FACE",FACE,{"disambiguationData":[OSD([sQuery(id+"F0.wireOp",EDGE,"E0"),sQuery(id+"F0.wireOp",EDGE,"E1"),sQuery(id+"F0.wireOp",EDGE,"E2"),sQuery(id+"F0.wireOp",EDGE,"E3.MirrorCS"),sQuery(id+"F0.wireOp",EDGE,"E4.1.0"),sQuery(id+"F0.wireOp",EDGE,"E4.1.1"),sQuery(id+"F0.wireOp",EDGE,"E4.2.0"),sQuery(id+"F0.wireOp",EDGE,"E4.2.1"),sQuery(id+"F0.wireOp",EDGE,"E5.trimOffspring"),sQuery(id+"F0.wireOp",EDGE,"E6.trimOffspring")])],"isStart":false})});
            var sketch = newSketch(context, id + "F12", { "sketchPlane" : qUnion([Q0])});
            skFitSpline(sketch, "E150", {"points": [v(-4.8, 29.25) * mm, v(-4.73, 29.03) * mm, v(-4.2, 28.63) * mm, v(-3.34, 28.17) * mm, v(-3.04, 27.94) * mm, v(-2.91, 27.94) * mm, v(-2.82, 27.98) * mm, v(-2.8, 28.13) * mm, v(-2.73, 28.2) * mm, v(-2.53, 28.17) * mm, v(-1.9, 28.03) * mm, v(-0.94, 28) * mm, v(-0.27, 28.2) * mm, v(0.18, 28.41) * mm, v(0.28, 28.6) * mm, v(0.19, 28.75) * mm, v(0.1, 28.78) * mm, v(0, 28.73) * mm, v(-0.39, 28.54) * mm, v(-0.66, 28.41) * mm, v(-1.1, 28.35) * mm, v(-1.41, 28.41) * mm, v(-1.48, 28.65) * mm, v(-1.41, 29.02) * mm, v(-1.22, 29.22) * mm, v(-1.04, 29.3) * mm, v(-1.2, 29.33) * mm, v(-1.63, 29.3) * mm, v(-1.84, 29.15) * mm, v(-2.28, 29.07) * mm, v(-2.83, 29.22) * mm, v(-3.2, 29.67) * mm, v(-3.3, 30.2) * mm, v(-3.37, 30.29) * mm, v(-3.38, 30.52) * mm, v(-3.14, 30.59) * mm, v(-2.89, 30.48) * mm, v(-2.61, 30.16) * mm, v(-2.22, 29.86) * mm, v(-2.06, 29.67) * mm, v(-1.6, 29.64) * mm, v(-1.29, 29.71) * mm, v(-1.23, 29.95) * mm, v(-1.37, 29.89) * mm, v(-1.55, 29.9) * mm, v(-1.94, 30.1) * mm, v(-2.2, 30.47) * mm, v(-2.33, 31.03) * mm, v(-2.33, 31.12) * mm, v(-2.43, 31.19) * mm, v(-2.44, 31.37) * mm, v(-2.25, 31.46) * mm, v(-1.69, 31.45) * mm, v(-1.47, 31.56) * mm, v(-1.11, 31.6) * mm, v(-0.83, 31.87) * mm, v(-0.46, 32.09) * mm, v(-0.21, 32.18) * mm, v(-0.2, 32.37) * mm, v(-0.28, 32.54) * mm, v(-0.33, 32.8) * mm, v(-0.15, 32.84) * mm, v(0, 32.73) * mm, v(0.19, 32.64) * mm, v(0.52, 32.77) * mm, v(0.64, 32.95) * mm, v(0.83, 33.17) * mm, v(1.03, 33.23) * mm, v(1.12, 33.01) * mm, v(1.2, 32.72) * mm, v(1.33, 32.67) * mm, v(1.56, 32.87) * mm, v(1.92, 32.94) * mm, v(2.29, 32.85) * mm, v(2.43, 32.87) * mm, v(2.64, 32.87) * mm, v(2.72, 32.7) * mm, v(2.4, 32.53) * mm, v(2, 32.32) * mm, v(2.16, 32.17) * mm, v(2.46, 32.14) * mm, v(2.87, 32.13) * mm, v(3.3, 32.16) * mm, v(3.37, 31.87) * mm, v(3, 31.42) * mm, v(3.05, 31.17) * mm, v(3.38, 30.78) * mm, v(3.5, 30.6) * mm, v(3.52, 30.42) * mm, v(3.34, 30.21) * mm, v(3.18, 29.99) * mm, v(2.89, 29.96) * mm, v(2.83, 29.85) * mm, v(3.1, 29.6) * mm, v(3.4, 29.3) * mm, v(3.57, 28.9) * mm, v(3.58, 28.57) * mm, v(3.44, 28.41) * mm, v(3.41, 28.23) * mm, v(3.57, 27.95) * mm, v(3.73, 27.76) * mm, v(3.74, 27.55) * mm, v(3.57, 27.43) * mm, v(3.19, 27.32) * mm, v(3.03, 27.3) * mm, v(3.1, 26.97) * mm, v(3.47, 26.51) * mm, v(3.86, 25.66) * mm, v(3.83, 25.1) * mm, v(3.71, 24.69) * mm, v(3.52, 24.6) * mm, v(3.55, 24.87) * mm, v(3.38, 25.25) * mm, v(2.95, 25.55) * mm, v(2.54, 25.63) * mm, v(2.34, 25.7) * mm, v(2.14, 25.8) * mm, v(2.11, 25.58) * mm, v(2.6, 24.85) * mm, v(4.53, 22.64) * mm, v(4.94, 22.4) * mm, v(5.2, 22.2) * mm, v(5.72, 21.75) * mm, v(6.16, 21.45) * mm, v(6.5, 21.3) * mm, v(6.99, 21.58) * mm, v(7.37, 22.13) * mm, v(7.27, 22.7) * mm, v(6.95, 22.97) * mm, v(6.52, 23.02) * mm, v(6.09, 23.02) * mm, v(5.94, 23.04) * mm, v(5.9, 23.26) * mm, v(5.6, 23.43) * mm, v(5.17, 23.44) * mm, v(4.62, 23.62) * mm, v(4.47, 24.04) * mm, v(4.52, 24.2) * mm, v(4.68, 24.18) * mm, v(4.94, 23.95) * mm, v(5.56, 24) * mm, v(5.97, 24.02) * mm, v(6.1, 24.17) * mm, v(5.8, 24.28) * mm, v(5.3, 24.3) * mm, v(5.16, 24.53) * mm, v(5.1, 24.91) * mm, v(5.47, 24.93) * mm, v(5.46, 25.05) * mm, v(4.54, 26.02) * mm, v(4.31, 26.89) * mm, v(4.35, 27.73) * mm, v(4.34, 28.3) * mm, v(4.16, 28.67) * mm, v(3.86, 29.17) * mm, v(3.66, 29.7) * mm, v(3.65, 30.05) * mm, v(3.88, 29.87) * mm, v(4.25, 29.47) * mm, v(4.38, 29.3) * mm, v(4.47, 29.61) * mm, v(4.25, 29.96) * mm, v(4.01, 30.27) * mm, v(3.93, 31.07) * mm, v(4.04, 31.38) * mm, v(4.53, 31.7) * mm, v(5, 31.87) * mm, v(5.28, 32.01) * mm, v(5.4, 32.16) * mm, v(5.4, 31.8) * mm, v(5.12, 31.44) * mm, v(4.82, 31.17) * mm, v(4.93, 30.73) * mm, v(5.75, 30.12) * mm, v(6.07, 29.6) * mm, v(6.07, 29.27) * mm, v(6.26, 29.16) * mm, v(6.58, 28.84) * mm, v(6.6, 28.17) * mm, v(6.28, 27.83) * mm, v(5.88, 27.82) * mm, v(5.4, 27.64) * mm, v(5.05, 27.29) * mm, v(4.97, 26.76) * mm, v(5.08, 26.21) * mm, v(5.5, 25.62) * mm, v(5.72, 25.56) * mm, v(5.9, 25.77) * mm, v(6.02, 26.08) * mm, v(6.08, 26.14) * mm, v(6.23, 25.85) * mm, v(6.36, 25.46) * mm, v(6.2, 25.17) * mm, v(6.27, 25.03) * mm, v(6.47, 24.85) * mm, v(6.96, 24.38) * mm, v(7.28, 23.92) * mm, v(7.38, 23.8) * mm, v(7.65, 23.8) * mm, v(7.57, 24.86) * mm, v(7.58, 25.1) * mm, v(7.8, 24.9) * mm, v(8.1, 24.46) * mm, v(8.13, 23.84) * mm, v(8.2, 23.7) * mm, v(8.3, 22.73) * mm, v(8.27, 22.56) * mm, v(8.12, 21.89) * mm, v(7.8, 21.44) * mm, v(7.19, 21.13) * mm, v(6.7, 20.99) * mm, v(6.29, 20.93) * mm, v(6.24, 20.79) * mm, v(6.56, 20.51) * mm, v(6.87, 20.5) * mm, v(7.03, 20.78) * mm, v(7.22, 20.84) * mm, v(7.36, 20.54) * mm, v(7.34, 20.1) * mm, v(7.34, 19.95) * mm, v(7.56, 19.61) * mm, v(7.75, 19.16) * mm, v(7.66, 18.45) * mm, v(7.55, 18.19) * mm, v(7.41, 18.15) * mm, v(7.44, 17.89) * mm, v(7.88, 17.47) * mm, v(7.85, 17.1) * mm, v(7.64, 16.9) * mm, v(7.05, 17) * mm, v(6.98, 17.32) * mm, v(6.84, 17.48) * mm, v(6.7, 17.25) * mm, v(6.75, 17) * mm, v(6.86, 16.6) * mm, v(6.82, 16.25) * mm, v(6.69, 16.09) * mm, v(6.69, 15.75) * mm, v(6.86, 15.65) * mm, v(6.74, 15.58) * mm, v(6.24, 15.58) * mm, v(5.87, 15.88) * mm, v(5.76, 15.84) * mm, v(5.39, 15.52) * mm, v(4.8, 15.36) * mm, v(4.55, 15.24) * mm, v(4.33, 15.17) * mm, v(4.33, 15.74) * mm, v(4.32, 16.32) * mm, v(4.49, 16.42) * mm, v(4.5, 16.69) * mm, v(4.2, 16.8) * mm, v(4.07, 16.6) * mm, v(3.88, 16.69) * mm, v(3.92, 17.02) * mm, v(4.38, 17.36) * mm, v(4.97, 17.42) * mm, v(5.31, 17.3) * mm, v(5.47, 17.17) * mm, v(5.73, 17.33) * mm, v(5.98, 17.75) * mm, v(5.96, 18.35) * mm, v(5.85, 18.48) * mm, v(5.75, 18.5) * mm, v(5.73, 18.68) * mm, v(5.02, 18.67) * mm, v(4.82, 18.58) * mm, v(4.62, 18.49) * mm, v(3.87, 18.48) * mm, v(3.74, 18.25) * mm, v(3.7, 17.4) * mm, v(3.36, 16.77) * mm, v(2.76, 16.62) * mm, v(1.95, 16.57) * mm, v(1.6, 16.55) * mm, v(1.34, 16.38) * mm, v(1.27, 16.13) * mm, v(1.24, 15.92) * mm, v(1.04, 16.02) * mm, v(0.9, 16.35) * mm, v(0.93, 16.69) * mm, v(1.35, 17) * mm, v(1.86, 17.03) * mm, v(2.23, 17.07) * mm, v(2.55, 17.26) * mm, v(2.87, 17.58) * mm, v(2.9, 17.8) * mm, v(2.66, 17.97) * mm, v(2.23, 17.84) * mm, v(1.93, 17.85) * mm, v(2.33, 18.18) * mm, v(2.62, 18.61) * mm, v(2.58, 19.23) * mm, v(2.47, 19.34) * mm, v(2.4, 19.67) * mm, v(2.27, 19.85) * mm, v(2.3, 20.3) * mm, v(2.65, 20.75) * mm, v(2.8, 21.04) * mm, v(2.58, 21.12) * mm, v(2.17, 21.07) * mm, v(1.22, 20.26) * mm, v(1.06, 20.06) * mm, v(1.13, 19.77) * mm, v(1.35, 19.6) * mm, v(1.38, 19.23) * mm, v(1.14, 18.96) * mm, v(1.1, 18.55) * mm, v(1.5, 18.33) * mm, v(1.57, 18.19) * mm, v(1.33, 18.06) * mm, v(1.04, 18.07) * mm, v(0.93, 17.87) * mm, v(1.1, 17.57) * mm, v(1.1, 17.32) * mm, v(0.99, 17.3) * mm, v(0.96, 17.12) * mm, v(0.77, 17.1) * mm, v(0.49, 17.29) * mm, v(0.42, 16.92) * mm, v(0.26, 16.57) * mm, v(0, 16.62) * mm, v(-0.14, 16.76) * mm, v(-0.25, 17.04) * mm, v(-0.36, 17.06) * mm, v(-0.48, 16.98) * mm, v(-0.4, 16.6) * mm, v(-0.47, 15.87) * mm, v(-0.86, 16.02) * mm, v(-1.07, 16.11) * mm, v(-1.25, 16.14) * mm, v(-1.33, 16.34) * mm, v(-1.38, 16.56) * mm, v(-1.53, 16.5) * mm, v(-2.17, 15.93) * mm, v(-2.6, 15.9) * mm, v(-2.93, 15.94) * mm, v(-2.97, 15.77) * mm, v(-2.9, 15.47) * mm, v(-3, 15.36) * mm, v(-3.22, 15.63) * mm, v(-3.27, 16.02) * mm, v(-3.48, 16.3) * mm, v(-3.68, 16.62) * mm, v(-3.9, 16.74) * mm, v(-4.16, 16.46) * mm, v(-4.24, 16.37) * mm, v(-4.34, 16.52) * mm, v(-4.38, 16.9) * mm, v(-3.96, 17.4) * mm, v(-3.45, 17.6) * mm, v(-3.38, 17.76) * mm, v(-3.62, 17.85) * mm, v(-3.76, 17.97) * mm, v(-3.84, 18.13) * mm, v(-3.58, 18.3) * mm, v(-3.58, 18.52) * mm, v(-3.65, 18.65) * mm, v(-3.78, 18.71) * mm, v(-3.52, 18.8) * mm, v(-3.18, 18.74) * mm, v(-2.7, 18.51) * mm, v(-2.46, 18.23) * mm, v(-2.48, 18.02) * mm, v(-2.2, 17.93) * mm, v(-1.91, 17.93) * mm, v(-1.47, 17.92) * mm, v(-0.91, 18.37) * mm, v(-0.67, 18.86) * mm, v(-0.7, 19.42) * mm, v(-0.98, 19.94) * mm, v(-1.3, 20.12) * mm, v(-1.58, 19.94) * mm, v(-1.86, 19.68) * mm, v(-2.31, 19.5) * mm, v(-2.52, 19.53) * mm, v(-2.66, 19.5) * mm, v(-2.71, 19.37) * mm, v(-3.03, 19.42) * mm, v(-3, 19.72) * mm, v(-2.88, 19.85) * mm, v(-3.14, 20.12) * mm, v(-3.48, 20.3) * mm, v(-3.83, 20.21) * mm, v(-3.93, 20.02) * mm, v(-4.28, 20.1) * mm, v(-4.11, 20.52) * mm, v(-3.58, 20.9) * mm, v(-3.24, 20.91) * mm, v(-3.12, 20.71) * mm, v(-2.84, 20.53) * mm, v(-2.38, 20.54) * mm, v(-2.16, 20.67) * mm, v(-2.28, 20.8) * mm, v(-2.65, 20.82) * mm, v(-2.8, 21.09) * mm, v(-2.63, 21.22) * mm, v(-2, 21.31) * mm, v(-1.24, 21.77) * mm, v(-0.63, 22.33) * mm, v(-0.43, 22.43) * mm, v(0.3, 22.43) * mm, v(1.13, 22.37) * mm, v(1.74, 22.5) * mm, v(1.96, 22.63) * mm, v(1.78, 22.93) * mm, v(1.24, 23.1) * mm, v(0.68, 23.24) * mm, v(0.57, 23.11) * mm, v(0.33, 23.04) * mm, v(0.16, 23.17) * mm, v(-0.08, 23.23) * mm, v(-0.2, 23) * mm, v(-0.5, 23.08) * mm, v(-0.98, 23.34) * mm, v(-1.23, 23.51) * mm, v(-1.23, 23.58) * mm, v(-1.4, 23.7) * mm, v(-1.64, 23.22) * mm, v(-1.72, 22.81) * mm, v(-2.1, 22.83) * mm, v(-2.5, 22.81) * mm, v(-2.87, 22.4) * mm, v(-3.17, 22.2) * mm, v(-3.43, 22.16) * mm, v(-3.45, 22.38) * mm, v(-3.75, 22.58) * mm, v(-3.8, 22.81) * mm, v(-4.02, 22.75) * mm, v(-4, 22.12) * mm, v(-4.1, 21.55) * mm, v(-4.16, 21.19) * mm, v(-4.28, 21.1) * mm, v(-4.54, 21.35) * mm, v(-4.95, 21.52) * mm, v(-5, 21.82) * mm, v(-4.9, 22.04) * mm, v(-4.9, 22.36) * mm, v(-5.26, 22.13) * mm, v(-5.55, 21.67) * mm, v(-5.69, 21.32) * mm, v(-5.97, 21.33) * mm, v(-6.37, 21.58) * mm, v(-6.6, 21.4) * mm, v(-6.62, 21.21) * mm, v(-6.7, 21.05) * mm, v(-6.91, 21.36) * mm, v(-6.91, 21.8) * mm, v(-6.47, 22.26) * mm, v(-5.83, 22.42) * mm, v(-5.67, 22.62) * mm, v(-6.05, 22.7) * mm, v(-6.3, 22.54) * mm, v(-6.74, 22.55) * mm, v(-6.82, 22.83) * mm, v(-7.06, 22.85) * mm, v(-7.34, 22.8) * mm, v(-7.45, 23.02) * mm, v(-7.02, 23.3) * mm, v(-6.84, 23.4) * mm, v(-6.77, 23.62) * mm, v(-6.53, 23.58) * mm, v(-6.25, 23.3) * mm, v(-6.12, 23.71) * mm, v(-6.43, 24.02) * mm, v(-6.5, 24.27) * mm, v(-6.1, 24.26) * mm, v(-5.65, 24.14) * mm, v(-5.25, 23.69) * mm, v(-4.98, 23.5) * mm, v(-4.54, 23.77) * mm, v(-3.7, 24.33) * mm, v(-2.9, 24.78) * mm, v(-2.67, 24.82) * mm, v(-2.35, 24.97) * mm, v(-2.72, 25.26) * mm, v(-3.29, 25.19) * mm, v(-3.53, 24.89) * mm, v(-3.73, 24.8) * mm, v(-3.89, 25.07) * mm, v(-3.88, 25.33) * mm, v(-4.23, 25.64) * mm, v(-4.82, 25.56) * mm, v(-5.05, 25.57) * mm, v(-4.9, 26.2) * mm, v(-4.7, 26.64) * mm, v(-5.07, 26.58) * mm, v(-5.3, 26.4) * mm, v(-5.54, 26.15) * mm, v(-5.76, 26.2) * mm, v(-5.45, 26.58) * mm, v(-5.33, 26.77) * mm, v(-5.49, 26.88) * mm, v(-5.87, 26.62) * mm, v(-6.16, 26.74) * mm, v(-5.92, 27.04) * mm, v(-5.57, 27.37) * mm, v(-5.98, 27.4) * mm, v(-6.15, 27.28) * mm, v(-6.3, 27.47) * mm, v(-6.2, 27.73) * mm, v(-5.68, 28.15) * mm, v(-5.57, 28.36) * mm, v(-5.83, 28.32) * mm, v(-5.96, 28.4) * mm, v(-5.83, 28.74) * mm, v(-6.12, 28.89) * mm, v(-6.92, 28.9) * mm, v(-7.25, 28.86) * mm, v(-7.36, 28.7) * mm, v(-7.63, 28.77) * mm, v(-7.68, 29.11) * mm, v(-7.48, 29.3) * mm, v(-7.33, 29.44) * mm, v(-7.48, 29.6) * mm, v(-7.51, 29.8) * mm, v(-7.47, 29.93) * mm, v(-7.67, 29.93) * mm, v(-7.71, 29.7) * mm, v(-7.92, 29.86) * mm, v(-7.94, 30.03) * mm, v(-7.72, 30.22) * mm, v(-7.41, 30.56) * mm, v(-7.08, 30.6) * mm, v(-6.72, 30.33) * mm, v(-6.46, 30.09) * mm, v(-6.24, 30.03) * mm, v(-6.33, 30.22) * mm, v(-6.65, 30.56) * mm, v(-6.63, 30.85) * mm, v(-6.42, 30.95) * mm, v(-6.1, 30.92) * mm, v(-6.08, 31.17) * mm, v(-6.26, 31.28) * mm, v(-6.21, 31.45) * mm, v(-5.8, 31.47) * mm, v(-5.53, 31.32) * mm, v(-5.44, 31.12) * mm, v(-5.42, 30.74) * mm, v(-5.42, 30.58) * mm, v(-5.44, 30.5) * mm, v(-5.24, 30.7) * mm, v(-5.06, 30.87) * mm, v(-4.95, 30.95) * mm, v(-5.06, 31.1) * mm, v(-5.09, 31.4) * mm, v(-4.98, 31.49) * mm, v(-4.55, 31.07) * mm, v(-4.55, 30.84) * mm, v(-4.43, 30.65) * mm, v(-4.3, 30.44) * mm, v(-4.34, 30.09) * mm, v(-4.71, 29.57) * mm, v(-4.8, 29.25) * mm]});
            skFitSpline(sketch, "E151", {"points": [v(4.92, 21.35) * mm, v(5.18, 20.53) * mm, v(5.26, 20.59) * mm, v(5.75, 21) * mm, v(5.43, 21.14) * mm, v(4.92, 21.35) * mm]});
            skFitSpline(sketch, "E152", {"points": [v(-0.72, 30.07) * mm, v(-0.61, 29.97) * mm, v(-0.47, 29.9) * mm, v(-0.3, 29.91) * mm, v(-0.17, 30.02) * mm, v(-0.24, 30.3) * mm, v(-0.24, 30.4) * mm, v(-0.47, 30.27) * mm, v(-0.72, 30.07) * mm]});
            skFitSpline(sketch, "E153", {"points": [v(-0.66, 31.18) * mm, v(-0.66, 31.4) * mm, v(-0.53, 31.4) * mm, v(-0.34, 31.35) * mm, v(-0.17, 31.24) * mm, v(-0.24, 31.14) * mm, v(-0.46, 31.06) * mm, v(-0.66, 31.18) * mm]});
            skFitSpline(sketch, "E154", {"points": [v(5.87, 28.92) * mm, v(5.37, 28.61) * mm, v(5.02, 28.31) * mm, v(5.32, 28.35) * mm, v(5.5, 28.46) * mm, v(5.86, 28.44) * mm, v(6.03, 28.66) * mm, v(5.87, 28.92) * mm]});
            skSolve(sketch);
        }
        {
            var Q0;
            Q0=qSketchRegion(id+"F12",true);
            extrude(context, id + "F13", {"entities" : qUnion([Q0]), "operationType" : NewBodyOperationType.REMOVE, "oppositeDirection" : true, "depth" : .75 * mm, "offsetDistance" : 25.4 * mm});
        }
        {
            var Q0;
            Q0=makeQuery(id+"F3.boolean.opBoolean","SPLIT",FACE,{"disambiguationData":[TD([makeQuery(id+"F3.opExtrude","SWEPT_FACE",FACE,{"disambiguationData":[OSD([sQuery(id+"F2.wireOp",EDGE,"E11")])]}),makeQuery(id+"F3.opExtrude","SWEPT_FACE",FACE,{"disambiguationData":[OSD([sQuery(id+"F2.wireOp",EDGE,"E29.trimOffspring")])]}),makeQuery(id+"F3.opExtrude","SWEPT_FACE",FACE,{"disambiguationData":[OSD([sQuery(id+"F2.wireOp",EDGE,"E30.trimOffspring")])]})])],"derivedFrom":makeQuery(id+"F1.opExtrude","CAP_FACE",FACE,{"disambiguationData":[OSD([sQuery(id+"F0.wireOp",EDGE,"E0"),sQuery(id+"F0.wireOp",EDGE,"E1"),sQuery(id+"F0.wireOp",EDGE,"E2"),sQuery(id+"F0.wireOp",EDGE,"E3.MirrorCS"),sQuery(id+"F0.wireOp",EDGE,"E4.1.0"),sQuery(id+"F0.wireOp",EDGE,"E4.1.1"),sQuery(id+"F0.wireOp",EDGE,"E4.2.0"),sQuery(id+"F0.wireOp",EDGE,"E4.2.1"),sQuery(id+"F0.wireOp",EDGE,"E5.trimOffspring"),sQuery(id+"F0.wireOp",EDGE,"E6.trimOffspring")])],"isStart":false})});
            var sketch = newSketch(context, id + "F14", { "sketchPlane" : qUnion([Q0])});
            skArc(sketch, "E155", {"start": v(19.8, -11.14) * mm, "mid": v(19.85, -9.45) * mm, "end": v(18.93, -8.03) * mm});
            skLineSegment(sketch, "E156", {"start": v(27.31, -16.54) * mm, "end": v(27.37, -16.64) * mm});
            skLineSegment(sketch, "E157", {"start": v(27.37, -16.64) * mm, "end": v(27.8, -15.9) * mm});
            skLineSegment(sketch, "E158", {"start": v(27.8, -15.9) * mm, "end": v(27.61, -15.92) * mm});
            skArc(sketch, "E159.trimOffspring", {"start": v(16.07, -12.85) * mm, "mid": v(17.81, -12.97) * mm, "end": v(19.3, -12.04) * mm});
            skArc(sketch, "E160.trimOffspring", {"start": v(18.02, -7.53) * mm, "mid": v(14.68, -8.8) * mm, "end": v(15.22, -12.32) * mm});
            skLineSegment(sketch, "E161", {"start": v(28.97, -14.54) * mm, "end": v(26.8, -18.26) * mm});
            skLineSegment(sketch, "E162", {"start": v(28.6, -18.08) * mm, "end": v(28.16, -18.62) * mm});
            skLineSegment(sketch, "E163", {"start": v(28.16, -18.62) * mm, "end": v(27.9, -18.41) * mm});
            skLineSegment(sketch, "E164", {"start": v(27.9, -18.41) * mm, "end": v(28.62, -17.22) * mm});
            skLineSegment(sketch, "E165", {"start": v(28.62, -17.22) * mm, "end": v(28.9, -17.39) * mm});
            skLineSegment(sketch, "E166", {"start": v(28.9, -17.39) * mm, "end": v(28.6, -17.87) * mm});
            skLineSegment(sketch, "E167.MirrorCS", {"start": v(29.24, -16.8) * mm, "end": v(29.52, -16.3) * mm});
            skLineSegment(sketch, "E168.MirrorCS", {"start": v(28.96, -16.65) * mm, "end": v(29.24, -16.8) * mm});
            skLineSegment(sketch, "E169.MirrorCS", {"start": v(29.64, -15.43) * mm, "end": v(28.96, -16.65) * mm});
            skLineSegment(sketch, "E170.MirrorCS", {"start": v(29.96, -15.56) * mm, "end": v(29.64, -15.43) * mm});
            skLineSegment(sketch, "E171.MirrorCS", {"start": v(29.71, -16.15) * mm, "end": v(29.96, -15.56) * mm});
            skFitSpline(sketch, "E172", {"points": [v(30.88, -18.16) * mm, v(28.62, -20.49) * mm, v(25.18, -21.45) * mm, v(21.92, -20.98) * mm, v(17.66, -18.85) * mm, v(13.94, -15.33) * mm, v(12.88, -12.58) * mm, v(13, -9.41) * mm, v(14.64, -6.7) * mm, v(17.3, -5.1) * mm, v(21, -5.01) * mm, v(25.04, -6.51) * mm, v(28.88, -9.12) * mm, v(31.16, -12.12) * mm, v(31.69, -14.67) * mm, v(31.45, -16.8) * mm, v(30.88, -18.16) * mm]});
            skFitSpline(sketch, "E173.0", {"points": [v(33.27, -19.13) * mm, v(33.04, -19.51) * mm, v(32.78, -19.9) * mm, v(32.39, -20.44) * mm, v(31.8, -21.13) * mm, v(31.1, -21.81) * mm, v(30.52, -22.27) * mm, v(30.16, -22.51) * mm, v(29.89, -22.7) * mm, v(29.6, -22.86) * mm, v(29.21, -23.06) * mm, v(28.73, -23.28) * mm, v(28.15, -23.5) * mm, v(27.37, -23.72) * mm, v(26.42, -23.9) * mm, v(25.5, -24) * mm, v(24.79, -24) * mm, v(24.08, -23.98) * mm, v(23.2, -23.9) * mm, v(22.16, -23.7) * mm, v(21.15, -23.4) * mm, v(20.12, -23.04) * mm, v(19.08, -22.6) * mm, v(18.04, -22.07) * mm, v(17, -21.46) * mm, v(15.96, -20.78) * mm, v(14.95, -20.02) * mm, v(14, -19.2) * mm, v(13.11, -18.34) * mm, v(12.3, -17.43) * mm, v(11.72, -16.62) * mm, v(11.33, -15.94) * mm, v(11, -15.26) * mm, v(10.73, -14.57) * mm, v(10.54, -13.88) * mm, v(10.4, -13.22) * mm, v(10.3, -12.55) * mm, v(10.25, -11.86) * mm, v(10.23, -11.33) * mm, v(10.24, -10.78) * mm, v(10.28, -10.22) * mm, v(10.35, -9.65) * mm, v(10.47, -9.06) * mm, v(10.63, -8.48) * mm, v(10.9, -7.73) * mm, v(11.33, -6.84) * mm, v(11.96, -5.88) * mm, v(12.7, -5.03) * mm, v(13.51, -4.26) * mm, v(14.44, -3.6) * mm, v(15.3, -3.14) * mm, v(16.02, -2.84) * mm, v(16.6, -2.65) * mm, v(17.17, -2.5) * mm, v(17.95, -2.37) * mm, v(18.93, -2.29) * mm, v(20.1, -2.32) * mm, v(21.25, -2.46) * mm, v(22.75, -2.79) * mm, v(24.17, -3.29) * mm, v(25.5, -3.9) * mm, v(26.48, -4.4) * mm, v(27.45, -4.94) * mm, v(28.4, -5.53) * mm, v(29.34, -6.2) * mm, v(30.24, -6.91) * mm, v(31.1, -7.7) * mm, v(31.87, -8.55) * mm, v(32.57, -9.45) * mm, v(33.17, -10.41) * mm, v(33.58, -11.27) * mm, v(33.82, -11.98) * mm, v(34.02, -12.67) * mm, v(34.17, -13.52) * mm, v(34.24, -14.5) * mm, v(34.22, -15.27) * mm, v(34.18, -15.87) * mm, v(34.13, -16.3) * mm, v(34.06, -16.72) * mm, v(33.99, -17.11) * mm, v(33.9, -17.5) * mm, v(33.8, -17.9) * mm, v(33.65, -18.3) * mm, v(33.48, -18.72) * mm, v(33.27, -19.13) * mm, v(33.04, -19.51) * mm, v(32.78, -19.9) * mm, v(33.27, -19.13) * mm]});
            skLineSegment(sketch, "E174", {"start": v(24.26, -4.3) * mm, "end": v(24.72, -4.47) * mm});
            skLineSegment(sketch, "E175", {"start": v(24.72, -4.47) * mm, "end": v(24.54, -4.93) * mm});
            skLineSegment(sketch, "E176", {"start": v(24.26, -4.3) * mm, "end": v(24.41, -3.91) * mm});
            skLineSegment(sketch, "E177", {"start": v(24.41, -3.91) * mm, "end": v(24.17, -3.82) * mm});
            skLineSegment(sketch, "E178", {"start": v(24.54, -4.93) * mm, "end": v(24.1, -4.76) * mm});
            skLineSegment(sketch, "E179", {"start": v(24.1, -4.76) * mm, "end": v(23.93, -5.18) * mm});
            skLineSegment(sketch, "E180", {"start": v(23.93, -5.18) * mm, "end": v(23.68, -5.08) * mm});
            skPoint(sketch, "E181.orphan", {"position": v(23.93, -3.73) * mm});
            skLineSegment(sketch, "E182.MirrorCS", {"start": v(23.79, -4.11) * mm, "end": v(23.33, -3.94) * mm});
            skLineSegment(sketch, "E183.MirrorCS", {"start": v(23.79, -4.11) * mm, "end": v(23.93, -3.73) * mm});
            skLineSegment(sketch, "E184.MirrorCS", {"start": v(23.93, -3.73) * mm, "end": v(24.17, -3.82) * mm});
            skLineSegment(sketch, "E185.MirrorCS", {"start": v(23.6, -4.57) * mm, "end": v(23.43, -4.98) * mm});
            skLineSegment(sketch, "E186.MirrorCS", {"start": v(23.43, -4.98) * mm, "end": v(23.68, -5.08) * mm});
            skLineSegment(sketch, "E187.MirrorCS", {"start": v(23.15, -4.4) * mm, "end": v(23.6, -4.57) * mm});
            skLineSegment(sketch, "E188.MirrorCS", {"start": v(23.33, -3.94) * mm, "end": v(23.15, -4.4) * mm});
            skLineSegment(sketch, "E189", {"start": v(15.68, -18.82) * mm, "end": v(16.02, -18.47) * mm});
            skLineSegment(sketch, "E190", {"start": v(16.02, -18.47) * mm, "end": v(15.86, -18.32) * mm});
            skLineSegment(sketch, "E191", {"start": v(15.68, -18.82) * mm, "end": v(16.08, -19.2) * mm});
            skLineSegment(sketch, "E192", {"start": v(16.08, -19.2) * mm, "end": v(15.77, -19.53) * mm});
            skLineSegment(sketch, "E193", {"start": v(15.77, -19.53) * mm, "end": v(15.37, -19.15) * mm});
            skLineSegment(sketch, "E194", {"start": v(15.37, -19.15) * mm, "end": v(15, -19.53) * mm});
            skLineSegment(sketch, "E195", {"start": v(15, -19.53) * mm, "end": v(14.84, -19.37) * mm});
            skPoint(sketch, "E196.orphan", {"position": v(15.7, -18.17) * mm});
            skPoint(sketch, "E197.orphan", {"position": v(14.68, -19.21) * mm});
            skLineSegment(sketch, "E198.MirrorCS", {"start": v(15.05, -18.84) * mm, "end": v(14.68, -19.21) * mm});
            skLineSegment(sketch, "E199.MirrorCS", {"start": v(14.68, -19.21) * mm, "end": v(14.84, -19.37) * mm});
            skLineSegment(sketch, "E200.MirrorCS", {"start": v(14.65, -18.45) * mm, "end": v(15.05, -18.84) * mm});
            skLineSegment(sketch, "E201.MirrorCS", {"start": v(14.96, -18.13) * mm, "end": v(14.65, -18.45) * mm});
            skLineSegment(sketch, "E202.MirrorCS", {"start": v(15.36, -18.52) * mm, "end": v(14.96, -18.13) * mm});
            skLineSegment(sketch, "E203.MirrorCS", {"start": v(15.36, -18.52) * mm, "end": v(15.7, -18.16) * mm});
            skLineSegment(sketch, "E204.MirrorCS", {"start": v(15.7, -18.16) * mm, "end": v(15.86, -18.32) * mm});
            skFitSpline(sketch, "E205.0", {"points": [v(33.71, -19.37) * mm, v(33.47, -19.78) * mm, v(33.2, -20.2) * mm, v(32.78, -20.76) * mm, v(32.3, -21.33) * mm, v(31.73, -21.9) * mm, v(31.26, -22.33) * mm, v(30.82, -22.67) * mm, v(30.45, -22.94) * mm, v(30.15, -23.13) * mm, v(29.84, -23.3) * mm, v(29.44, -23.52) * mm, v(28.92, -23.75) * mm, v(28.3, -23.98) * mm, v(27.5, -24.22) * mm, v(26.69, -24.37) * mm, v(25.91, -24.46) * mm, v(25.34, -24.5) * mm, v(24.78, -24.51) * mm, v(24.04, -24.5) * mm, v(23.12, -24.4) * mm, v(22.04, -24.19) * mm, v(21, -23.9) * mm, v(19.94, -23.51) * mm, v(18.87, -23.06) * mm, v(17.8, -22.52) * mm, v(16.73, -21.9) * mm, v(15.67, -21.2) * mm, v(14.64, -20.42) * mm, v(13.66, -19.58) * mm, v(12.74, -18.7) * mm, v(12.05, -17.9) * mm, v(11.54, -17.24) * mm, v(11.2, -16.72) * mm, v(10.88, -16.18) * mm, v(10.61, -15.64) * mm, v(10.38, -15.1) * mm, v(10.2, -14.55) * mm, v(10.05, -14) * mm, v(9.9, -13.3) * mm, v(9.8, -12.61) * mm, v(9.74, -11.9) * mm, v(9.72, -11.33) * mm, v(9.73, -10.75) * mm, v(9.77, -10.17) * mm, v(9.85, -9.56) * mm, v(9.97, -8.95) * mm, v(10.14, -8.33) * mm, v(10.43, -7.53) * mm, v(10.88, -6.6) * mm, v(11.55, -5.58) * mm, v(12.32, -4.68) * mm, v(13.19, -3.87) * mm, v(14.17, -3.16) * mm, v(15.07, -2.68) * mm, v(15.85, -2.36) * mm, v(16.45, -2.17) * mm, v(17.07, -2.01) * mm, v(17.89, -1.87) * mm, v(18.91, -1.78) * mm, v(20.13, -1.8) * mm, v(21.34, -1.96) * mm, v(22.9, -2.3) * mm, v(24.36, -2.81) * mm, v(25.73, -3.44) * mm, v(26.73, -3.95) * mm, v(27.7, -4.5) * mm, v(28.69, -5.11) * mm, v(29.64, -5.78) * mm, v(30.57, -6.53) * mm, v(31.45, -7.34) * mm, v(32.26, -8.22) * mm, v(32.99, -9.16) * mm, v(33.62, -10.17) * mm, v(34.05, -11.08) * mm, v(34.3, -11.82) * mm, v(34.51, -12.56) * mm, v(34.68, -13.46) * mm, v(34.75, -14.49) * mm, v(34.73, -15.3) * mm, v(34.68, -15.91) * mm, v(34.63, -16.37) * mm, v(34.56, -16.8) * mm, v(34.49, -17.21) * mm, v(34.4, -17.62) * mm, v(34.28, -18.05) * mm, v(34.13, -18.49) * mm, v(33.94, -18.94) * mm, v(33.71, -19.37) * mm, v(33.47, -19.78) * mm, v(33.2, -20.2) * mm, v(33.71, -19.37) * mm]});
            skFitSpline(sketch, "E206.0", {"points": [v(31.65, -17.86) * mm, v(31.33, -18.42) * mm, v(30.89, -19.06) * mm, v(30.32, -19.74) * mm, v(29.63, -20.4) * mm, v(28.84, -20.98) * mm, v(27.96, -21.42) * mm, v(26.75, -21.81) * mm, v(25.22, -22.01) * mm, v(23.5, -21.92) * mm, v(21.78, -21.5) * mm, v(19.95, -20.8) * mm, v(18.38, -19.94) * mm, v(17.14, -19.12) * mm, v(15.92, -18.2) * mm, v(14.53, -16.94) * mm, v(13.26, -15.36) * mm, v(12.68, -14.06) * mm, v(12.42, -13) * mm, v(12.26, -11.9) * mm, v(12.24, -10.72) * mm, v(12.43, -9.53) * mm, v(12.8, -8.38) * mm, v(13.4, -7.34) * mm, v(14.16, -6.44) * mm, v(15.02, -5.64) * mm, v(16.02, -5) * mm, v(17.14, -4.6) * mm, v(18.35, -4.34) * mm, v(19.62, -4.3) * mm, v(20.9, -4.46) * mm, v(22.17, -4.74) * mm, v(23.72, -5.28) * mm, v(25.53, -6.16) * mm, v(27.3, -7.2) * mm, v(28.94, -8.43) * mm, v(30.13, -9.61) * mm, v(30.9, -10.62) * mm, v(31.39, -11.4) * mm, v(31.76, -12.19) * mm, v(32, -12.98) * mm, v(32.15, -13.77) * mm, v(32.2, -14.54) * mm, v(32.19, -15.3) * mm, v(32.12, -16.04) * mm, v(32, -16.71) * mm, v(31.86, -17.3) * mm, v(31.65, -17.86) * mm, v(31.33, -18.42) * mm, v(30.89, -19.06) * mm, v(31.65, -17.86) * mm]});
            skArc(sketch, "E207.0", {"start": v(20.38, -11.63) * mm, "mid": v(14.05, -8.46) * mm, "end": v(20, -12.3) * mm});
            skLineSegment(sketch, "E208.0", {"start": v(17.8, -9.94) * mm, "end": v(19.8, -11.14) * mm});
            skLineSegment(sketch, "E209.0", {"start": v(18.93, -8.03) * mm, "end": v(17.8, -9.94) * mm});
            skLineSegment(sketch, "E210.0", {"start": v(17.25, -10.86) * mm, "end": v(19.3, -12.04) * mm});
            skLineSegment(sketch, "E211.0", {"start": v(17.25, -10.86) * mm, "end": v(16.07, -12.85) * mm});
            skLineSegment(sketch, "E212.0", {"start": v(18.02, -7.53) * mm, "end": v(15.22, -12.32) * mm});
            skLineSegment(sketch, "E213.0", {"start": v(20.38, -11.63) * mm, "end": v(24.69, -14.19) * mm});
            skLineSegment(sketch, "E214.0", {"start": v(20, -12.3) * mm, "end": v(24.32, -14.81) * mm});
            skLineSegment(sketch, "E215.0", {"start": v(24.32, -14.81) * mm, "end": v(23.03, -17.04) * mm});
            skLineSegment(sketch, "E216.0", {"start": v(24.95, -15.17) * mm, "end": v(23.65, -17.4) * mm});
            skLineSegment(sketch, "E217.0", {"start": v(25.3, -14.55) * mm, "end": v(26.64, -12.31) * mm});
            skLineSegment(sketch, "E218.0", {"start": v(24.69, -14.19) * mm, "end": v(26.04, -11.91) * mm});
            skLineSegment(sketch, "E219.0", {"start": v(24.95, -15.17) * mm, "end": v(27.31, -16.54) * mm});
            skLineSegment(sketch, "E220.0", {"start": v(25.3, -14.55) * mm, "end": v(27.61, -15.92) * mm});
            skLineSegment(sketch, "E221.0", {"start": v(22.27, -17.36) * mm, "end": v(23.65, -18.16) * mm});
            skLineSegment(sketch, "E222.0", {"start": v(27.26, -12.06) * mm, "end": v(26.04, -11.16) * mm});
            skLineSegment(sketch, "E223.0", {"start": v(26.04, -11.91) * mm, "end": v(26.04, -11.16) * mm});
            skLineSegment(sketch, "E224.0", {"start": v(26.64, -12.31) * mm, "end": v(27.26, -12.06) * mm});
            skLineSegment(sketch, "E225.0", {"start": v(23.03, -17.04) * mm, "end": v(22.27, -17.36) * mm});
            skLineSegment(sketch, "E226.0", {"start": v(23.65, -18.16) * mm, "end": v(23.65, -17.4) * mm});
            skLineSegment(sketch, "E227.0", {"start": v(28.97, -14.54) * mm, "end": v(31.19, -15.44) * mm});
            skLineSegment(sketch, "E228.0", {"start": v(26.8, -18.26) * mm, "end": v(28.67, -19.75) * mm});
            skLineSegment(sketch, "E229.0", {"start": v(28.67, -19.75) * mm, "end": v(29.15, -19.14) * mm});
            skLineSegment(sketch, "E230.0", {"start": v(29.15, -19.14) * mm, "end": v(28.73, -18.8) * mm});
            skLineSegment(sketch, "E231.0", {"start": v(28.73, -18.8) * mm, "end": v(29.03, -18.43) * mm});
            skLineSegment(sketch, "E232.0", {"start": v(29.03, -18.43) * mm, "end": v(28.6, -18.08) * mm});
            skLineSegment(sketch, "E233.0", {"start": v(28.6, -17.87) * mm, "end": v(29.12, -18.2) * mm});
            skLineSegment(sketch, "E234.0", {"start": v(29.12, -18.2) * mm, "end": v(29.39, -17.75) * mm});
            skLineSegment(sketch, "E235.0", {"start": v(29.39, -17.75) * mm, "end": v(29.73, -17.96) * mm});
            skLineSegment(sketch, "E236.0", {"start": v(29.73, -17.96) * mm, "end": v(30.1, -17.7) * mm});
            skLineSegment(sketch, "E237.0", {"start": v(30.14, -17.25) * mm, "end": v(30.1, -17.7) * mm});
            skLineSegment(sketch, "E238.0", {"start": v(29.8, -17.05) * mm, "end": v(30.14, -17.25) * mm});
            skLineSegment(sketch, "E239.0", {"start": v(30.05, -16.6) * mm, "end": v(29.8, -17.05) * mm});
            skLineSegment(sketch, "E240.0", {"start": v(29.52, -16.3) * mm, "end": v(30.05, -16.6) * mm});
            skLineSegment(sketch, "E241.0", {"start": v(31.19, -15.44) * mm, "end": v(30.91, -16.12) * mm});
            skLineSegment(sketch, "E242.0", {"start": v(30.4, -15.92) * mm, "end": v(30.23, -16.37) * mm});
            skLineSegment(sketch, "E243", {"start": v(29.71, -16.15) * mm, "end": v(30.23, -16.37) * mm});
            skLineSegment(sketch, "E244", {"start": v(30.4, -15.92) * mm, "end": v(30.91, -16.12) * mm});
            skSolve(sketch);
        }
        {
            var Q0;
            Q0=qSketchRegion(id+"F14",true);
            var Q1;
            Q1=makeQuery(id+"F14.imprint","IMPRINT",FACE,{"disambiguationData":[TD([[makeQuery(id+"F14.imprint","IMPRINT",EDGE,{"derivedFrom":sQuery(id+"F14.wireOp",EDGE,"E174")}),-1.0]])]});
            var Q2;
            Q2=makeQuery(id+"F14.imprint","IMPRINT",FACE,{"disambiguationData":[TD([[makeQuery(id+"F14.imprint","IMPRINT",EDGE,{"derivedFrom":sQuery(id+"F14.wireOp",EDGE,"E189")}),1.0]])]});
            var Q3;
            Q3=makeQuery(id+"F14.imprint","IMPRINT",FACE,{"disambiguationData":[TD([[makeQuery(id+"F14.imprint","IMPRINT",EDGE,{"derivedFrom":sQuery(id+"F14.wireOp",EDGE,"E172")}),1.0]])]});
            var Q4;
            Q4=makeQuery(id+"F14.imprint","IMPRINT",FACE,{"disambiguationData":[TD([[makeQuery(id+"F14.imprint","IMPRINT",EDGE,{"derivedFrom":sQuery(id+"F14.wireOp",EDGE,"E155")}),-1.0]])]});
            var Q5;
            Q5=makeQuery(id+"F14.imprint","IMPRINT",FACE,{"disambiguationData":[TD([[makeQuery(id+"F14.imprint","IMPRINT",EDGE,{"derivedFrom":sQuery(id+"F14.wireOp",EDGE,"E161")}),1.0]])]});
            extrude(context, id + "F15", {"entities" : qUnion([Q0, Q1, Q2, Q3, Q4, Q5]), "operationType" : NewBodyOperationType.REMOVE, "oppositeDirection" : true, "depth" : .5 * mm, "offsetDistance" : 25.4 * mm});
        }
        {
            var Q0;
            Q0=qCreatedBy(makeId("Top.planeOp"),FACE);
            var sketch = newSketch(context, id + "F16", { "sketchPlane" : qUnion([Q0])});
            skArc(sketch, "E245.0.0", {"start": v(30.98, -2.94) * mm, "mid": v(26.95, 15.56) * mm, "end": v(12.95, 28.3) * mm});
            skArc(sketch, "E245.0.1", {"start": v(12.95, 28.3) * mm, "mid": v(12.51, 29.3) * mm, "end": v(12.05, 30.3) * mm});
            skArc(sketch, "E245.0.2", {"start": v(-12.05, 30.3) * mm, "mid": v(-12.51, 29.3) * mm, "end": v(-12.95, 28.3) * mm});
            skArc(sketch, "E245.0.3", {"start": v(-12.95, 28.3) * mm, "mid": v(-26.95, 15.56) * mm, "end": v(-30.98, -2.94) * mm});
            skArc(sketch, "E245.0.4", {"start": v(-30.98, -2.94) * mm, "mid": v(-31.64, -3.82) * mm, "end": v(-32.27, -4.71) * mm});
            skArc(sketch, "E245.0.5", {"start": v(-20.22, -25.6) * mm, "mid": v(-19.12, -25.5) * mm, "end": v(-18.03, -25.36) * mm});
            skArc(sketch, "E245.0.6", {"start": v(-18.03, -25.36) * mm, "mid": v(0, -31.12) * mm, "end": v(18.03, -25.36) * mm});
            skArc(sketch, "E245.0.7", {"start": v(18.03, -25.36) * mm, "mid": v(19.12, -25.5) * mm, "end": v(20.22, -25.6) * mm});
            skArc(sketch, "E245.0.8", {"start": v(32.27, -4.71) * mm, "mid": v(31.64, -3.82) * mm, "end": v(30.98, -2.94) * mm});
            skArc(sketch, "E246.0", {"start": v(-12.05, 30.3) * mm, "mid": v(-28.25, 16.3) * mm, "end": v(-32.27, -4.71) * mm});
            skArc(sketch, "E247.0", {"start": v(32.27, -4.71) * mm, "mid": v(28.25, 16.3) * mm, "end": v(12.05, 30.3) * mm});
            skArc(sketch, "E248.0", {"start": v(-20.22, -25.6) * mm, "mid": v(0, -32.62) * mm, "end": v(20.22, -25.6) * mm});
            skPoint(sketch, "E249.orphan", {"position": v(0, 44.92) * mm});
            skPoint(sketch, "E250.orphan", {"position": v(-38.9, -22.46) * mm});
            skPoint(sketch, "E251.orphan", {"position": v(38.9, -22.46) * mm});
            skSolve(sketch);
        }
        {
            var Q0;
            Q0=qSketchRegion(id+"F16",true);
            var Q1;
            Q1=makeQuery(id+"F3.opExtrude","CAP_FACE",FACE,{"disambiguationData":[OSD([sQuery(id+"F2.wireOp",EDGE,"E7.0.1"),sQuery(id+"F2.wireOp",EDGE,"E7.0.4"),sQuery(id+"F2.wireOp",EDGE,"E7.0.7"),sQuery(id+"F2.wireOp",EDGE,"E8.2"),sQuery(id+"F2.wireOp",EDGE,"E8.3"),sQuery(id+"F2.wireOp",EDGE,"E8.7"),sQuery(id+"F2.wireOp",EDGE,"E9"),sQuery(id+"F2.wireOp",EDGE,"E10"),sQuery(id+"F2.wireOp",EDGE,"E11"),sQuery(id+"F2.wireOp",EDGE,"E12.0"),sQuery(id+"F2.wireOp",EDGE,"E13.0"),sQuery(id+"F2.wireOp",EDGE,"E14.0"),sQuery(id+"F2.wireOp",EDGE,"E17.trimOffspring"),sQuery(id+"F2.wireOp",EDGE,"E18.trimOffspring"),sQuery(id+"F2.wireOp",EDGE,"E19.trimOffspring"),sQuery(id+"F2.wireOp",EDGE,"E20.trimOffspring"),sQuery(id+"F2.wireOp",EDGE,"E21.trimOffspring"),sQuery(id+"F2.wireOp",EDGE,"E22.trimOffspring"),sQuery(id+"F2.wireOp",EDGE,"E23.trimOffspring"),sQuery(id+"F2.wireOp",EDGE,"E24.trimOffspring"),sQuery(id+"F2.wireOp",EDGE,"E25.trimOffspring"),sQuery(id+"F2.wireOp",EDGE,"E26.trimOffspring"),sQuery(id+"F2.wireOp",EDGE,"E27.trimOffspring"),sQuery(id+"F2.wireOp",EDGE,"E28.trimOffspring"),sQuery(id+"F2.wireOp",EDGE,"E29.trimOffspring"),sQuery(id+"F2.wireOp",EDGE,"E30.trimOffspring"),sQuery(id+"F2.wireOp",EDGE,"E33.trimOffspring"),sQuery(id+"F2.wireOp",EDGE,"E34.trimOffspring"),sQuery(id+"F2.wireOp",EDGE,"E37.trimOffspring"),sQuery(id+"F2.wireOp",EDGE,"E38.trimOffspring")])],"isStart":false});
            extrude(context, id + "F17", {"entities" : qUnion([Q0]), "operationType" : NewBodyOperationType.ADD, "endBound" : BoundingType.UP_TO_SURFACE, "depth" : 25.4 * mm, "endBoundEntityFace" : qUnion([Q1]), "offsetDistance" : 25.4 * mm});
        }
        {
            var Q0;
            Q0=qCreatedBy(makeId("Top.planeOp"),FACE);
            var sketch = newSketch(context, id + "F18", { "sketchPlane" : qUnion([Q0])});
            skPoint(sketch, "E252.0", {"position": v(21.26, 6) * mm});
            skCircle(sketch, "E253.0", {"center": v(-21.21, 12.25) * mm, "radius": 6.4 * mm});
            skCircle(sketch, "E254.0", {"center": v(21.21, 12.25) * mm, "radius": 6.4 * mm});
            skCircle(sketch, "E255.0", {"center": v(0, -24.5) * mm, "radius": 6.4 * mm});
            skSolve(sketch);
        }
        {
            var Q0;
            Q0=qSketchRegion(id+"F18",true);
            extrude(context, id + "F19", {"entities" : qUnion([Q0]), "operationType" : NewBodyOperationType.REMOVE, "depth" : 25.4 * mm, "offsetDistance" : 25.4 * mm});
        }
    });
